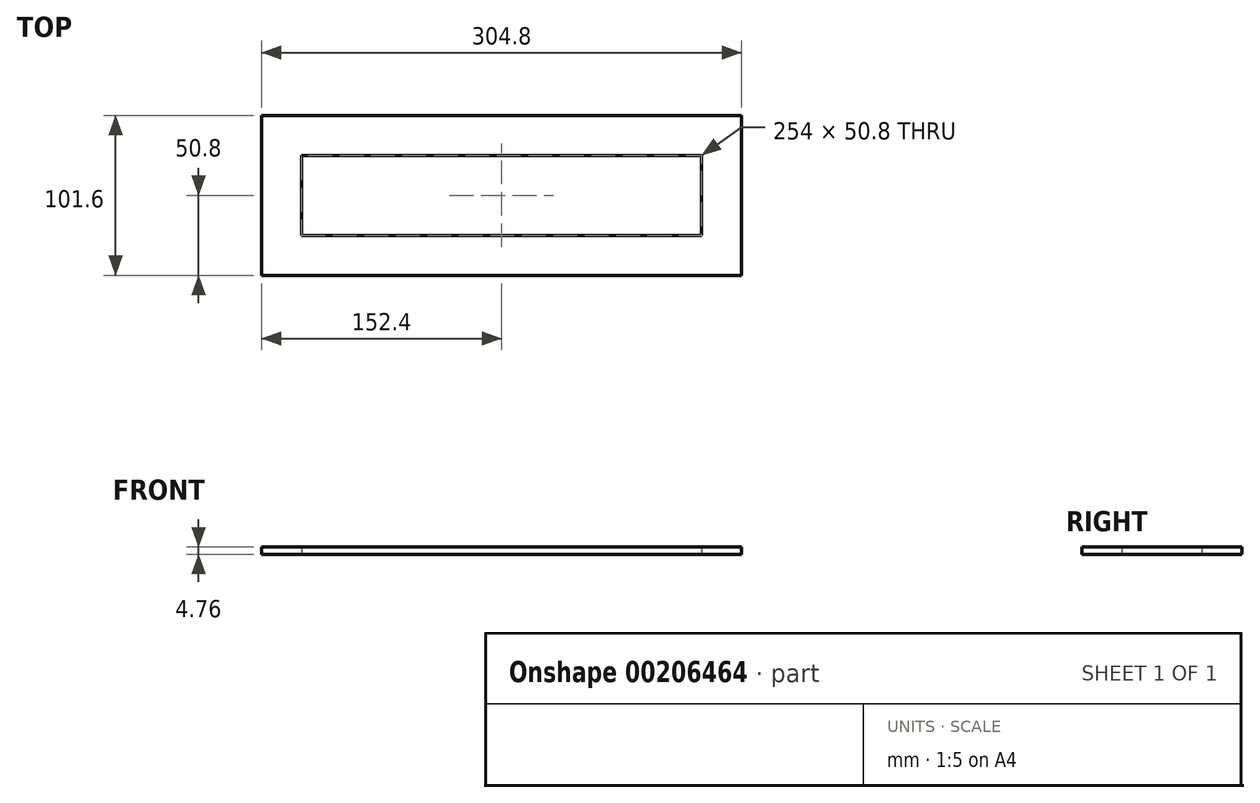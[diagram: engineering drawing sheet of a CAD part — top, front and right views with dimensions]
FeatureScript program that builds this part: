
annotation { "Feature Type Name" : "Feature", "Feature Type Description" : "" }
export const myFeature = defineFeature(function(context is Context, id is Id, definition is map)
    precondition{}
    {
        {
            var Q0;
            Q0=qCreatedBy(makeId("Top.planeOp"),FACE);
            var sketch = newSketch(context, id + "F0", { "sketchPlane" : qUnion([Q0])});
            skLineSegment(sketch, "E0.bottom", {"start": v(0, 0) * mm, "end": v(304.8, 0) * mm});
            skLineSegment(sketch, "E0.top", {"start": v(0, 101.6) * mm, "end": v(304.8, 101.6) * mm});
            skLineSegment(sketch, "E0.left", {"start": v(0, 0) * mm, "end": v(0, 101.6) * mm});
            skLineSegment(sketch, "E0.right", {"start": v(304.8, 0) * mm, "end": v(304.8, 101.6) * mm});
            skLineSegment(sketch, "E1.0", {"start": v(25.4, 25.4) * mm, "end": v(279.4, 25.4) * mm});
            skLineSegment(sketch, "E1.1", {"start": v(25.4, 25.4) * mm, "end": v(25.4, 76.2) * mm});
            skLineSegment(sketch, "E1.2", {"start": v(25.4, 76.2) * mm, "end": v(279.4, 76.2) * mm});
            skLineSegment(sketch, "E1.3", {"start": v(279.4, 25.4) * mm, "end": v(279.4, 76.2) * mm});
            skSolve(sketch);
        }
        {
            var Q0;
            Q0 = qSketchRegion(id + "F0", true);
            extrude(context, id + "F1", {"entities" : qUnion([Q0]), "endBound" : BoundingType.SYMMETRIC, "depth" : 4.76 * mm});
        }
    });
